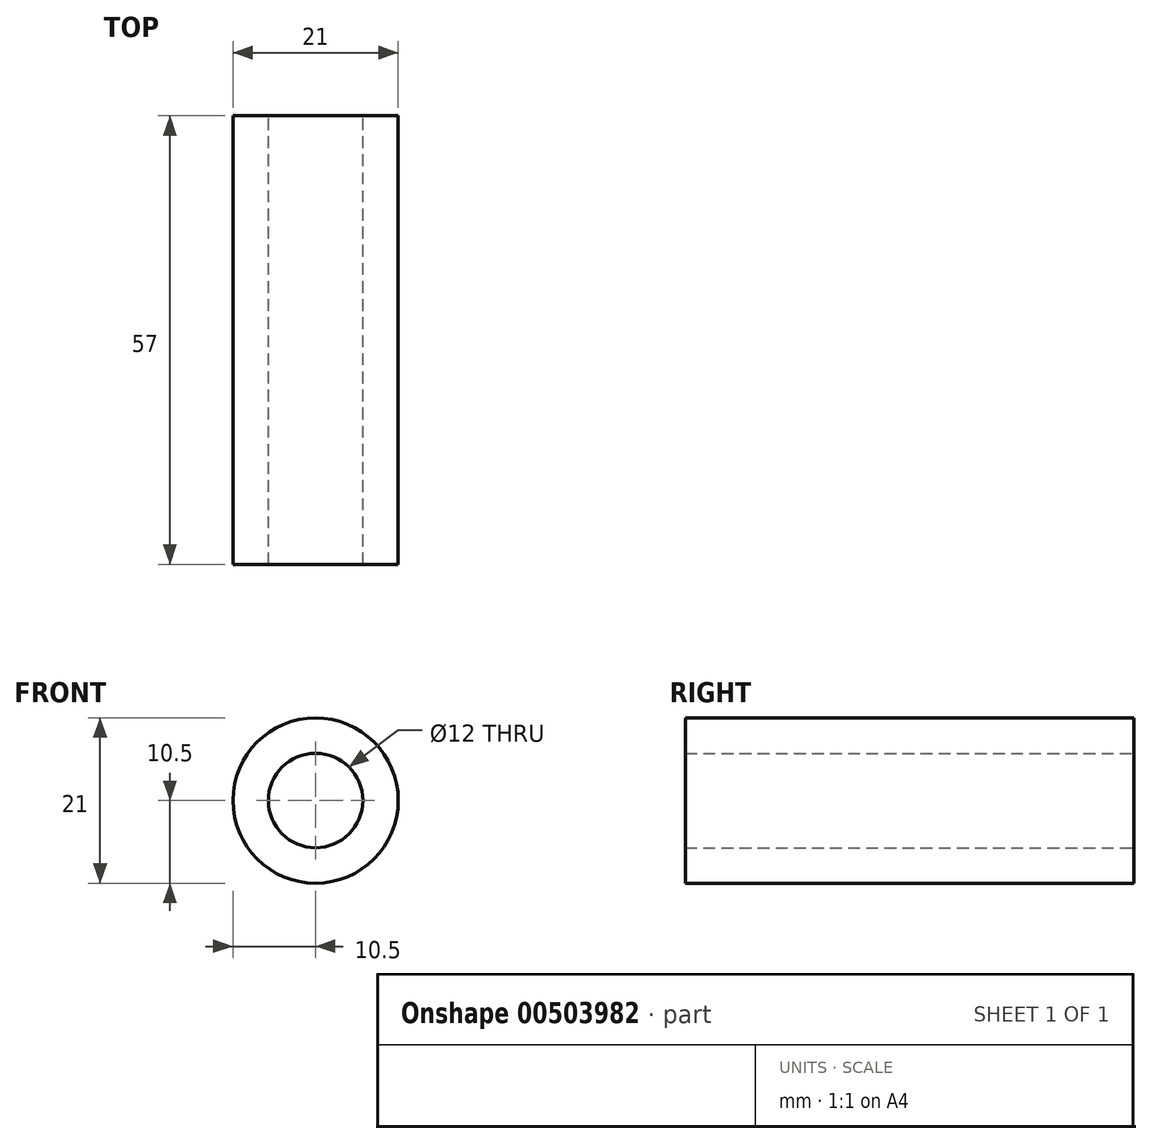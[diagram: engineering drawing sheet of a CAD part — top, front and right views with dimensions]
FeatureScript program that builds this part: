
annotation { "Feature Type Name" : "Feature", "Feature Type Description" : "" }
export const myFeature = defineFeature(function(context is Context, id is Id, definition is map)
    precondition{}
    {
        {
            var Q0;
            Q0=qCreatedBy(makeId("Front.planeOp"),FACE);
            var sketch = newSketch(context, id + "F0", { "sketchPlane" : qUnion([Q0])});
            skCircle(sketch, "E0", {"center": v(0, 0) * mm, "radius": 6 * mm});
            skCircle(sketch, "E1", {"center": v(0, 0) * mm, "radius": 10.5 * mm});
            skSolve(sketch);
        }
        {
            var Q0;
            Q0=makeQuery(id+"F0.imprint","IMPRINT",FACE,{"disambiguationData":[TD([[makeQuery(id+"F0.imprint","IMPRINT",EDGE,{"derivedFrom":sQuery(id+"F0.wireOp",EDGE,"E0")}),-1.0]])]});
            extrude(context, id + "F1", {"entities" : qUnion([Q0]), "depth" : 57 * mm});
        }
    });
